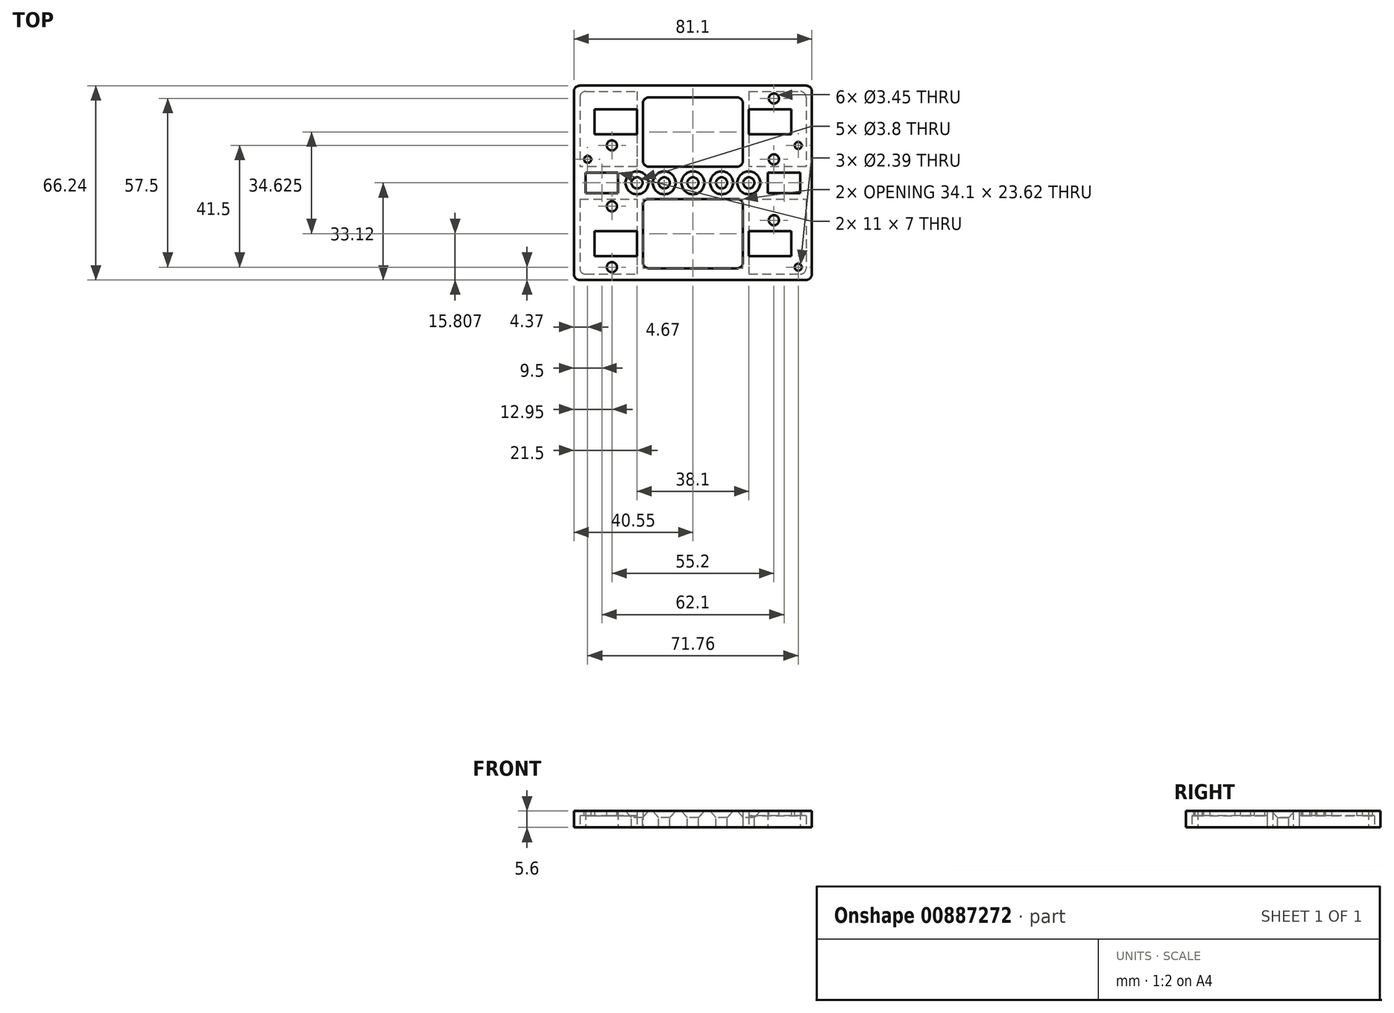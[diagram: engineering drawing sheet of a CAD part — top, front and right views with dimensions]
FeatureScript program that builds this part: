
annotation { "Feature Type Name" : "Feature", "Feature Type Description" : "" }
export const myFeature = defineFeature(function(context is Context, id is Id, definition is map)
    precondition{}
    {
        {
            var Q0;
            Q0=qCreatedBy(makeId("Top.planeOp"),FACE);
            var sketch = newSketch(context, id + "F0", { "sketchPlane" : qUnion([Q0])});
            skLineSegment(sketch, "E0.top", {"start": v(-38.55, -31.12) * mm, "end": v(38.55, -31.12) * mm, "construction": true});
            skLineSegment(sketch, "E0.left", {"start": v(-38.55, 31.12) * mm, "end": v(-38.55, -31.13) * mm, "construction": true});
            skLineSegment(sketch, "E0.right", {"start": v(38.55, 31.12) * mm, "end": v(38.55, -31.12) * mm, "construction": true});
            skLineSegment(sketch, "E1.left", {"start": v(-40.55, 33.12) * mm, "end": v(-40.55, -33.12) * mm});
            skLineSegment(sketch, "E2", {"start": v(-38.55, 31.12) * mm, "end": v(38.55, 31.12) * mm, "construction": true});
            skLineSegment(sketch, "E3", {"start": v(-40.55, -33.12) * mm, "end": v(40.55, -33.12) * mm});
            skLineSegment(sketch, "E4", {"start": v(40.55, 33.13) * mm, "end": v(40.55, -33.12) * mm});
            skLineSegment(sketch, "E5", {"start": v(-40.55, 33.12) * mm, "end": v(40.55, 33.13) * mm});
            skSolve(sketch);
        }
        {
            var Q0;
            Q0=makeQuery(id+"F0.imprint","IMPRINT",FACE,{"disambiguationData":[TD([[makeQuery(id+"F0.imprint","IMPRINT",EDGE,{"derivedFrom":sQuery(id+"F0.wireOp",EDGE,"E1.left")}),1.0]])]});
            extrude(context, id + "F1", {"entities" : qUnion([Q0]), "depth" : 5.6 * mm, "offsetDistance" : 25 * mm});
        }
        {
            var Q0;
            Q0=makeQuery(id+"F1.opExtrude","CAP_FACE",FACE,{"disambiguationData":[OSD([sQuery(id+"F0.wireOp",EDGE,"E1.left"),sQuery(id+"F0.wireOp",EDGE,"E3"),sQuery(id+"F0.wireOp",EDGE,"E4"),sQuery(id+"F0.wireOp",EDGE,"E5")])],"isStart":false});
            var sketch = newSketch(context, id + "F2", { "sketchPlane" : qUnion([Q0])});
            skLineSegment(sketch, "E6.bottom", {"start": v(35.88, 12.75) * mm, "end": v(-27.6, 12.75) * mm, "construction": true});
            skLineSegment(sketch, "E6.top", {"start": v(27.6, 28.75) * mm, "end": v(-27.6, 28.75) * mm, "construction": true});
            skLineSegment(sketch, "E6.right", {"start": v(-27.6, 12.75) * mm, "end": v(-27.6, 28.75) * mm, "construction": true});
            skLineSegment(sketch, "E7.top", {"start": v(27.6, 8) * mm, "end": v(-27.6, 8) * mm, "construction": true});
            skLineSegment(sketch, "E7.right", {"start": v(-27.6, -8) * mm, "end": v(-27.6, 8) * mm, "construction": true});
            skLineSegment(sketch, "E8.bottom", {"start": v(35.88, -28.75) * mm, "end": v(-27.6, -28.75) * mm, "construction": true});
            skLineSegment(sketch, "E8.top", {"start": v(27.6, -12.75) * mm, "end": v(-27.6, -12.75) * mm, "construction": true});
            skLineSegment(sketch, "E8.right", {"start": v(-27.6, -28.75) * mm, "end": v(-27.6, -12.75) * mm, "construction": true});
            skLineSegment(sketch, "E9", {"start": v(-27.6, -12.75) * mm, "end": v(-27.6, -10.38) * mm, "construction": true});
            skLineSegment(sketch, "E10", {"start": v(-27.6, -10.38) * mm, "end": v(-27.6, -8) * mm, "construction": true});
            skLineSegment(sketch, "E11", {"start": v(-27.6, 8) * mm, "end": v(-27.6, 10.37) * mm, "construction": true});
            skLineSegment(sketch, "E12", {"start": v(-27.6, 10.37) * mm, "end": v(-27.6, 12.75) * mm, "construction": true});
            skLineSegment(sketch, "E13", {"start": v(-27.6, 28.75) * mm, "end": v(-27.6, 31.12) * mm, "construction": true});
            skLineSegment(sketch, "E14", {"start": v(-27.6, 28.75) * mm, "end": v(-38.55, 28.75) * mm, "construction": true});
            skLineSegment(sketch, "E15", {"start": v(-27.6, -28.75) * mm, "end": v(-27.6, -31.12) * mm, "construction": true});
            skLineSegment(sketch, "E16", {"start": v(27.6, 28.75) * mm, "end": v(38.55, 28.75) * mm, "construction": true});
            skLineSegment(sketch, "E17", {"start": v(-27.6, 8) * mm, "end": v(-35.88, 8) * mm, "construction": true});
            skLineSegment(sketch, "E18.0", {"start": v(-38.55, 31.12) * mm, "end": v(38.55, 31.12) * mm, "construction": true});
            skLineSegment(sketch, "E19.0", {"start": v(-38.55, 31.12) * mm, "end": v(-38.55, -31.13) * mm, "construction": true});
            skLineSegment(sketch, "E20.0", {"start": v(-38.55, -31.12) * mm, "end": v(38.55, -31.12) * mm, "construction": true});
            skLineSegment(sketch, "E21.0", {"start": v(38.55, 31.12) * mm, "end": v(38.55, -31.12) * mm, "construction": true});
            skSolve(sketch);
        }
        {
            var Q0;
            Q0=sQuery(id+"F2.wireOp",VERTEX,"E6.bottom.end");
            var Q1;
            Q1=sQuery(id+"F2.wireOp",VERTEX,"E6.top.start");
            var Q2;
            Q2=sQuery(id+"F2.wireOp",VERTEX,"E7.right.start");
            var Q3;
            Q3=sQuery(id+"F2.wireOp",VERTEX,"E7.top.start");
            var Q4;
            Q4=sQuery(id+"F2.wireOp",VERTEX,"E8.top.start");
            var Q5;
            Q5=sQuery(id+"F2.wireOp",VERTEX,"E8.bottom.end");
            var Q6;
            Q6=makeQuery(id+"F1.opExtrude","SWEPT_BODY",BODY,{"disambiguationData":[OSD([sQuery(id+"F0.wireOp",EDGE,"E1.left"),sQuery(id+"F0.wireOp",EDGE,"E3"),sQuery(id+"F0.wireOp",EDGE,"E4"),sQuery(id+"F0.wireOp",EDGE,"E5")])]});
            hole(context, id + "F3", {"style" : HoleStyle.SIMPLE, "endStyle" : HoleEndStyle.THROUGH, "holeDiameter" : 3.45 * mm, "majorDiameter" : 5 * mm, "isTappedThrough" : true, "tappedDepth" : 12 * mm, "tapClearance" : 3, "locations" : qUnion([Q0, Q1, Q2, Q3, Q4, Q5]), "scope" : qUnion([Q6])});
        }
        {
            var Q0;
            Q0=sQuery(id+"F2.wireOp",VERTEX,"E17.end");
            var Q1;
            Q1=sQuery(id+"F2.wireOp",VERTEX,"E6.bottom.start");
            var Q2;
            Q2=sQuery(id+"F2.wireOp",VERTEX,"E8.bottom.start");
            var Q3;
            Q3=makeQuery(id+"F1.opExtrude","SWEPT_BODY",BODY,{"disambiguationData":[OSD([sQuery(id+"F0.wireOp",EDGE,"E1.left"),sQuery(id+"F0.wireOp",EDGE,"E3"),sQuery(id+"F0.wireOp",EDGE,"E4"),sQuery(id+"F0.wireOp",EDGE,"E5")])]});
            hole(context, id + "F4", {"style" : HoleStyle.SIMPLE, "endStyle" : HoleEndStyle.THROUGH, "holeDiameter" : 2.4 * mm, "majorDiameter" : 5 * mm, "isTappedThrough" : true, "tappedDepth" : 12 * mm, "tapClearance" : 3, "locations" : qUnion([Q0, Q1, Q2]), "scope" : qUnion([Q3])});
        }
        {
            var Q0;
            Q0=makeQuery(id+"F1.opExtrude","CAP_FACE",FACE,{"disambiguationData":[OSD([sQuery(id+"F0.wireOp",EDGE,"E1.left"),sQuery(id+"F0.wireOp",EDGE,"E3"),sQuery(id+"F0.wireOp",EDGE,"E4"),sQuery(id+"F0.wireOp",EDGE,"E5")])],"isStart":false});
            var sketch = newSketch(context, id + "F5", { "sketchPlane" : qUnion([Q0])});
            skPoint(sketch, "E22.middle", {"position": v(0, 0) * mm});
            skLineSegment(sketch, "E23", {"start": v(-9.78, 0) * mm, "end": v(9.78, 0) * mm, "construction": true});
            skLineSegment(sketch, "E24", {"start": v(-9.78, 0) * mm, "end": v(-19.05, 0) * mm, "construction": true});
            skLineSegment(sketch, "E25", {"start": v(9.78, 0) * mm, "end": v(19.05, 0) * mm, "construction": true});
            skSolve(sketch);
        }
        {
            var Q0;
            Q0=sQuery(id+"F5.wireOp",VERTEX,"E22.middle");
            var Q1;
            Q1=sQuery(id+"F5.wireOp",VERTEX,"E23.start");
            var Q2;
            Q2=sQuery(id+"F5.wireOp",VERTEX,"E23.end");
            var Q3;
            Q3=sQuery(id+"F5.wireOp",VERTEX,"E25.end");
            var Q4;
            Q4=sQuery(id+"F5.wireOp",VERTEX,"E24.end");
            var Q5;
            Q5=makeQuery(id+"F1.opExtrude","SWEPT_BODY",BODY,{"disambiguationData":[OSD([sQuery(id+"F0.wireOp",EDGE,"E1.left"),sQuery(id+"F0.wireOp",EDGE,"E3"),sQuery(id+"F0.wireOp",EDGE,"E4"),sQuery(id+"F0.wireOp",EDGE,"E5")])]});
            hole(context, id + "F6", {"style" : HoleStyle.C_SINK, "endStyle" : HoleEndStyle.THROUGH, "holeDiameter" : 3.8 * mm, "cSinkDiameter" : 7.8 * mm, "cSinkAngle" : 82 * degree, "majorDiameter" : 3.5 * mm, "isTappedThrough" : true, "tappedDepth" : 12 * mm, "tapClearance" : 3, "locations" : qUnion([Q0, Q1, Q2, Q3, Q4]), "scope" : qUnion([Q5])});
        }
        {
            var Q0;
            Q0=makeQuery(id+"F0.imprint","IMPRINT",FACE,{"disambiguationData":[TD([[makeQuery(id+"F0.imprint","IMPRINT",EDGE,{"derivedFrom":sQuery(id+"F0.wireOp",EDGE,"E1.left")}),1.0]])]});
            var sketch = newSketch(context, id + "F7", { "sketchPlane" : qUnion([Q0])});
            skLineSegment(sketch, "E26.0", {"start": v(-38.55, -31.12) * mm, "end": v(38.55, -31.12) * mm});
            skLineSegment(sketch, "E27.0", {"start": v(-38.55, 31.12) * mm, "end": v(-38.55, -31.13) * mm});
            skLineSegment(sketch, "E28.0", {"start": v(-38.55, 31.12) * mm, "end": v(38.55, 31.12) * mm});
            skLineSegment(sketch, "E29.0", {"start": v(38.55, 31.12) * mm, "end": v(38.55, -31.12) * mm});
            skLineSegment(sketch, "E30", {"start": v(-38.55, 0) * mm, "end": v(38.55, 0) * mm, "construction": true});
            skLineSegment(sketch, "E31", {"start": v(-38.55, -5.5) * mm, "end": v(38.55, -5.5) * mm});
            skLineSegment(sketch, "E32", {"start": v(38.55, 5.5) * mm, "end": v(-38.55, 5.5) * mm});
            skLineSegment(sketch, "E33.bottom", {"start": v(-33.5, -25) * mm, "end": v(33.5, -25) * mm});
            skLineSegment(sketch, "E33.top", {"start": v(-33.5, -16.5) * mm, "end": v(33.5, -16.5) * mm});
            skLineSegment(sketch, "E33.left", {"start": v(-33.5, -25) * mm, "end": v(-33.5, -16.5) * mm});
            skLineSegment(sketch, "E33.right", {"start": v(33.5, -25) * mm, "end": v(33.5, -16.5) * mm});
            skLineSegment(sketch, "E34.bottom", {"start": v(-33.5, 16.5) * mm, "end": v(33.5, 16.5) * mm});
            skLineSegment(sketch, "E34.top", {"start": v(-33.5, 25) * mm, "end": v(33.5, 25) * mm});
            skLineSegment(sketch, "E34.left", {"start": v(-33.5, 16.5) * mm, "end": v(-33.5, 25) * mm});
            skLineSegment(sketch, "E34.right", {"start": v(33.5, 16.5) * mm, "end": v(33.5, 25) * mm});
            skLineSegment(sketch, "E35", {"start": v(19.88, -5.5) * mm, "end": v(19.88, 0) * mm, "construction": true});
            skLineSegment(sketch, "E36", {"start": v(19.88, 0) * mm, "end": v(19.88, 5.5) * mm, "construction": true});
            skPoint(sketch, "E37.0", {"position": v(-27.6, -20.75) * mm});
            skPoint(sketch, "E38.0", {"position": v(-27.6, 20.75) * mm});
            skLineSegment(sketch, "E39", {"start": v(-27.6, 20.75) * mm, "end": v(-33.5, 20.75) * mm, "construction": true});
            skLineSegment(sketch, "E40", {"start": v(-33.5, 20.75) * mm, "end": v(-38.55, 20.75) * mm, "construction": true});
            skLineSegment(sketch, "E41", {"start": v(33.5, 20.75) * mm, "end": v(38.55, 20.75) * mm, "construction": true});
            skLineSegment(sketch, "E42", {"start": v(-27.6, -20.75) * mm, "end": v(-33.5, -20.75) * mm, "construction": true});
            skLineSegment(sketch, "E43", {"start": v(-17.05, 31.12) * mm, "end": v(-17.05, -31.12) * mm});
            skLineSegment(sketch, "E44", {"start": v(-19.05, 31.12) * mm, "end": v(-19.05, -31.12) * mm});
            skLineSegment(sketch, "E45", {"start": v(17.05, 31.12) * mm, "end": v(17.05, -31.12) * mm});
            skLineSegment(sketch, "E46", {"start": v(19.05, 31.12) * mm, "end": v(19.05, -31.12) * mm});
            skLineSegment(sketch, "E47", {"start": v(0, 31.12) * mm, "end": v(0, -31.12) * mm, "construction": true});
            skLineSegment(sketch, "E48", {"start": v(-17.05, 27.34) * mm, "end": v(0, 27.34) * mm, "construction": true});
            skLineSegment(sketch, "E49", {"start": v(0, 27.34) * mm, "end": v(17.05, 27.34) * mm, "construction": true});
            skLineSegment(sketch, "E50.bottom", {"start": v(-36.55, -3.5) * mm, "end": v(-25.55, -3.5) * mm});
            skLineSegment(sketch, "E50.top", {"start": v(-36.55, 3.5) * mm, "end": v(-25.55, 3.5) * mm});
            skLineSegment(sketch, "E50.left", {"start": v(-36.55, -3.5) * mm, "end": v(-36.55, 3.5) * mm});
            skLineSegment(sketch, "E50.right", {"start": v(-25.55, -3.5) * mm, "end": v(-25.55, 3.5) * mm});
            skLineSegment(sketch, "E51.bottom", {"start": v(36.55, -3.5) * mm, "end": v(25.55, -3.5) * mm});
            skLineSegment(sketch, "E51.top", {"start": v(36.55, 3.5) * mm, "end": v(25.55, 3.5) * mm});
            skLineSegment(sketch, "E51.left", {"start": v(36.55, -3.5) * mm, "end": v(36.55, 3.5) * mm});
            skLineSegment(sketch, "E51.right", {"start": v(25.55, -3.5) * mm, "end": v(25.55, 3.5) * mm});
            skPoint(sketch, "E52", {"position": v(-36.55, 0) * mm});
            skLineSegment(sketch, "E53", {"start": v(-17.05, 29.12) * mm, "end": v(17.05, 29.12) * mm});
            skLineSegment(sketch, "E54", {"start": v(-17.05, -29.12) * mm, "end": v(17.05, -29.12) * mm});
            skSolve(sketch);
        }
        {
            var Q0;
            {var subQ0=sQuery(id+"F7.wireOp",EDGE,"E33.left");Q0=makeQuery(id+"F7.imprint","IMPRINT",FACE,{"disambiguationData":[TD([[makeQuery(id+"F7.imprint","IMPRINT",EDGE,{"derivedFrom":subQ0}),1.0]])]});}
            var Q1;
            {var subQ0=sQuery(id+"F7.wireOp",EDGE,"E34.left");Q1=makeQuery(id+"F7.imprint","IMPRINT",FACE,{"disambiguationData":[TD([[makeQuery(id+"F7.imprint","IMPRINT",EDGE,{"derivedFrom":subQ0}),1.0]])]});}
            var Q2;
            {var subQ7=sQuery(id+"F7.wireOp",EDGE,"E34.right");Q2=makeQuery(id+"F7.imprint","IMPRINT",FACE,{"disambiguationData":[TD([[makeQuery(id+"F7.imprint","IMPRINT",EDGE,{"derivedFrom":subQ7}),-1.0]])]});}
            var Q3;
            {var subQ0=sQuery(id+"F7.wireOp",EDGE,"E33.right");Q3=makeQuery(id+"F7.imprint","IMPRINT",FACE,{"disambiguationData":[TD([[makeQuery(id+"F7.imprint","IMPRINT",EDGE,{"derivedFrom":subQ0}),-1.0]])]});}
            var Q4;
            Q4=makeQuery(id+"F1.opExtrude","CAP_FACE",FACE,{"disambiguationData":[OSD([sQuery(id+"F0.wireOp",EDGE,"E1.left"),sQuery(id+"F0.wireOp",EDGE,"E3"),sQuery(id+"F0.wireOp",EDGE,"E4"),sQuery(id+"F0.wireOp",EDGE,"E5")])],"isStart":false});
            extrude(context, id + "F8", {"entities" : qUnion([Q0, Q1, Q2, Q3]), "operationType" : NewBodyOperationType.REMOVE, "endBound" : BoundingType.UP_TO_SURFACE, "depth" : 25 * mm, "endBoundEntityFace" : qUnion([Q4]), "hasOffset" : true, "offsetDistance" : 1.6 * mm});
        }
        {
            var Q0;
            {var subQ0=sQuery(id+"F7.wireOp",EDGE,"E43");var subQ1=sQuery(id+"F7.wireOp",EDGE,"E33.bottom");var subQ2=makeQuery(id+"F7.imprint","INTERSECT",VERTEX,{"derivedFrom":[subQ1,subQ0]});Q0=makeQuery(id+"F7.imprint","IMPRINT",FACE,{"disambiguationData":[TD([[makeQuery(id+"F7.imprint","IMPRINT",EDGE,{"disambiguationData":[TD([[subQ2,-1.0]])],"derivedFrom":subQ1}),1.0]])]});}
            var Q1;
            {var subQ0=sQuery(id+"F7.wireOp",EDGE,"E43");var subQ1=sQuery(id+"F7.wireOp",EDGE,"E34.bottom");var subQ2=makeQuery(id+"F7.imprint","INTERSECT",VERTEX,{"derivedFrom":[subQ1,subQ0]});Q1=makeQuery(id+"F7.imprint","IMPRINT",FACE,{"disambiguationData":[TD([[makeQuery(id+"F7.imprint","IMPRINT",EDGE,{"disambiguationData":[TD([[subQ2,-1.0]])],"derivedFrom":subQ1}),1.0]])]});}
            var Q2;
            {var subQ0=sQuery(id+"F7.wireOp",EDGE,"E33.left");Q2=makeQuery(id+"F7.imprint","IMPRINT",FACE,{"disambiguationData":[TD([[makeQuery(id+"F7.imprint","IMPRINT",EDGE,{"derivedFrom":subQ0}),-1.0]])]});}
            var Q3;
            {var subQ0=sQuery(id+"F7.wireOp",EDGE,"E33.right");Q3=makeQuery(id+"F7.imprint","IMPRINT",FACE,{"disambiguationData":[TD([[makeQuery(id+"F7.imprint","IMPRINT",EDGE,{"derivedFrom":subQ0}),1.0]])]});}
            var Q4;
            {var subQ0=sQuery(id+"F7.wireOp",EDGE,"E34.right");Q4=makeQuery(id+"F7.imprint","IMPRINT",FACE,{"disambiguationData":[TD([[makeQuery(id+"F7.imprint","IMPRINT",EDGE,{"derivedFrom":subQ0}),1.0]])]});}
            var Q5;
            {var subQ0=sQuery(id+"F7.wireOp",EDGE,"E34.left");Q5=makeQuery(id+"F7.imprint","IMPRINT",FACE,{"disambiguationData":[TD([[makeQuery(id+"F7.imprint","IMPRINT",EDGE,{"derivedFrom":subQ0}),-1.0]])]});}
            var Q6;
            {var subQ0=sQuery(id+"F7.wireOp",EDGE,"E45");var subQ1=sQuery(id+"F7.wireOp",EDGE,"E32");var subQ2=makeQuery(id+"F7.imprint","INTERSECT",VERTEX,{"derivedFrom":[subQ1,subQ0]});Q6=makeQuery(id+"F7.imprint","IMPRINT",FACE,{"disambiguationData":[TD([[makeQuery(id+"F7.imprint","IMPRINT",EDGE,{"disambiguationData":[TD([[subQ2,-1.0]])],"derivedFrom":subQ1}),-1.0]])]});}
            var Q7;
            {var subQ0=sQuery(id+"F7.wireOp",EDGE,"E43");var subQ1=sQuery(id+"F7.wireOp",EDGE,"E31");var subQ2=makeQuery(id+"F7.imprint","INTERSECT",VERTEX,{"derivedFrom":[subQ1,subQ0]});Q7=makeQuery(id+"F7.imprint","IMPRINT",FACE,{"disambiguationData":[TD([[makeQuery(id+"F7.imprint","IMPRINT",EDGE,{"disambiguationData":[TD([[subQ2,-1.0]])],"derivedFrom":subQ1}),-1.0]])]});}
            var Q8;
            Q8=makeQuery(id+"F7.imprint","IMPRINT",FACE,{"disambiguationData":[TD([[makeQuery(id+"F7.imprint","IMPRINT",EDGE,{"derivedFrom":sQuery(id+"F7.wireOp",EDGE,"E50.bottom")}),1.0]])]});
            var Q9;
            Q9=makeQuery(id+"F7.imprint","IMPRINT",FACE,{"disambiguationData":[TD([[makeQuery(id+"F7.imprint","IMPRINT",EDGE,{"derivedFrom":sQuery(id+"F7.wireOp",EDGE,"E51.bottom")}),-1.0]])]});
            var Q10;
            {var subQ5=sQuery(id+"F7.wireOp",EDGE,"E53");Q10=makeQuery(id+"F7.imprint","IMPRINT",FACE,{"disambiguationData":[TD([[makeQuery(id+"F7.imprint","IMPRINT",EDGE,{"derivedFrom":subQ5}),-1.0]])]});}
            var Q11;
            {var subQ5=sQuery(id+"F7.wireOp",EDGE,"E54");Q11=makeQuery(id+"F7.imprint","IMPRINT",FACE,{"disambiguationData":[TD([[makeQuery(id+"F7.imprint","IMPRINT",EDGE,{"derivedFrom":subQ5}),1.0]])]});}
            var Q12;
            Q12=makeQuery(id+"F1.opExtrude","CAP_FACE",FACE,{"disambiguationData":[OSD([sQuery(id+"F0.wireOp",EDGE,"E1.left"),sQuery(id+"F0.wireOp",EDGE,"E3"),sQuery(id+"F0.wireOp",EDGE,"E4"),sQuery(id+"F0.wireOp",EDGE,"E5")])],"isStart":false});
            extrude(context, id + "F9", {"entities" : qUnion([Q0, Q1, Q2, Q3, Q4, Q5, Q6, Q7, Q8, Q9, Q10, Q11]), "operationType" : NewBodyOperationType.REMOVE, "endBound" : BoundingType.UP_TO_SURFACE, "depth" : 25 * mm, "endBoundEntityFace" : qUnion([Q12]), "offsetDistance" : 25 * mm});
        }
        {
            var Q0;
            Q0=makeQuery(id+"F1.opExtrude","SWEPT_EDGE",EDGE,{"disambiguationData":[OSD([sQuery(id+"F0.wireOp",EDGE,"E1.left"),sQuery(id+"F0.wireOp",EDGE,"E5")])]});
            var Q1;
            Q1=makeQuery(id+"F1.opExtrude","SWEPT_EDGE",EDGE,{"disambiguationData":[OSD([sQuery(id+"F0.wireOp",EDGE,"E4"),sQuery(id+"F0.wireOp",EDGE,"E5")])]});
            var Q2;
            Q2=makeQuery(id+"F1.opExtrude","SWEPT_EDGE",EDGE,{"disambiguationData":[OSD([sQuery(id+"F0.wireOp",EDGE,"E3"),sQuery(id+"F0.wireOp",EDGE,"E4")])]});
            var Q3;
            Q3=makeQuery(id+"F1.opExtrude","SWEPT_EDGE",EDGE,{"disambiguationData":[OSD([sQuery(id+"F0.wireOp",EDGE,"E1.left"),sQuery(id+"F0.wireOp",EDGE,"E3")])]});
            var Q4;
            Q4=makeQuery(id+"F9.boolean.opBoolean","COPY",EDGE,{"derivedFrom":makeQuery(id+"F9.opExtrude","SWEPT_EDGE",EDGE,{"disambiguationData":[OSD([sQuery(id+"F7.wireOp",EDGE,"E28.0"),sQuery(id+"F7.wireOp",EDGE,"E43")])]})});
            var Q5;
            Q5=makeQuery(id+"F9.boolean.opBoolean","COPY",EDGE,{"derivedFrom":makeQuery(id+"F9.opExtrude","SWEPT_EDGE",EDGE,{"disambiguationData":[OSD([sQuery(id+"F7.wireOp",EDGE,"E28.0"),sQuery(id+"F7.wireOp",EDGE,"E45")])]})});
            var Q6;
            Q6=makeQuery(id+"F9.boolean.opBoolean","COPY",EDGE,{"derivedFrom":makeQuery(id+"F9.opExtrude","SWEPT_EDGE",EDGE,{"disambiguationData":[OSD([sQuery(id+"F7.wireOp",EDGE,"E32"),sQuery(id+"F7.wireOp",EDGE,"E43")])]})});
            var Q7;
            Q7=makeQuery(id+"F9.boolean.opBoolean","COPY",EDGE,{"derivedFrom":makeQuery(id+"F9.opExtrude","SWEPT_EDGE",EDGE,{"disambiguationData":[OSD([sQuery(id+"F7.wireOp",EDGE,"E32"),sQuery(id+"F7.wireOp",EDGE,"E45")])]})});
            var Q8;
            Q8=makeQuery(id+"F9.boolean.opBoolean","COPY",EDGE,{"derivedFrom":makeQuery(id+"F9.opExtrude","SWEPT_EDGE",EDGE,{"disambiguationData":[OSD([sQuery(id+"F7.wireOp",EDGE,"E31"),sQuery(id+"F7.wireOp",EDGE,"E43")])]})});
            var Q9;
            Q9=makeQuery(id+"F9.boolean.opBoolean","COPY",EDGE,{"derivedFrom":makeQuery(id+"F9.opExtrude","SWEPT_EDGE",EDGE,{"disambiguationData":[OSD([sQuery(id+"F7.wireOp",EDGE,"E31"),sQuery(id+"F7.wireOp",EDGE,"E45")])]})});
            var Q10;
            Q10=makeQuery(id+"F9.boolean.opBoolean","COPY",EDGE,{"derivedFrom":makeQuery(id+"F9.opExtrude","SWEPT_EDGE",EDGE,{"disambiguationData":[OSD([sQuery(id+"F7.wireOp",EDGE,"E26.0"),sQuery(id+"F7.wireOp",EDGE,"E45")])]})});
            var Q11;
            Q11=makeQuery(id+"F9.boolean.opBoolean","COPY",EDGE,{"derivedFrom":makeQuery(id+"F9.opExtrude","SWEPT_EDGE",EDGE,{"disambiguationData":[OSD([sQuery(id+"F7.wireOp",EDGE,"E26.0"),sQuery(id+"F7.wireOp",EDGE,"E43")])]})});
            var Q12;
            Q12=makeQuery(id+"F8.boolean.opBoolean","COPY",EDGE,{"derivedFrom":makeQuery(id+"F8.opExtrude","SWEPT_EDGE",EDGE,{"disambiguationData":[OSD([sQuery(id+"F7.wireOp",EDGE,"E28.0"),sQuery(id+"F7.wireOp",EDGE,"E29.0")])]})});
            var Q13;
            Q13=makeQuery(id+"F8.boolean.opBoolean","COPY",EDGE,{"derivedFrom":makeQuery(id+"F8.opExtrude","SWEPT_EDGE",EDGE,{"disambiguationData":[OSD([sQuery(id+"F7.wireOp",EDGE,"E26.0"),sQuery(id+"F7.wireOp",EDGE,"E29.0")])]})});
            var Q14;
            Q14=makeQuery(id+"F8.boolean.opBoolean","COPY",EDGE,{"derivedFrom":makeQuery(id+"F8.opExtrude","SWEPT_EDGE",EDGE,{"disambiguationData":[OSD([sQuery(id+"F7.wireOp",EDGE,"E27.0"),sQuery(id+"F7.wireOp",EDGE,"E28.0")])]})});
            var Q15;
            Q15=makeQuery(id+"F8.boolean.opBoolean","COPY",EDGE,{"derivedFrom":makeQuery(id+"F8.opExtrude","SWEPT_EDGE",EDGE,{"disambiguationData":[OSD([sQuery(id+"F7.wireOp",EDGE,"E26.0"),sQuery(id+"F7.wireOp",EDGE,"E27.0")])]})});
            fillet(context, id + "F10", {"entities" : qUnion([Q0, Q1, Q2, Q3, Q4, Q5, Q6, Q7, Q8, Q9, Q10, Q11, Q12, Q13, Q14, Q15]), "radius" : 2 * mm, "tangentPropagation" : true, "allowEdgeOverflow" : false});
        }
    });
